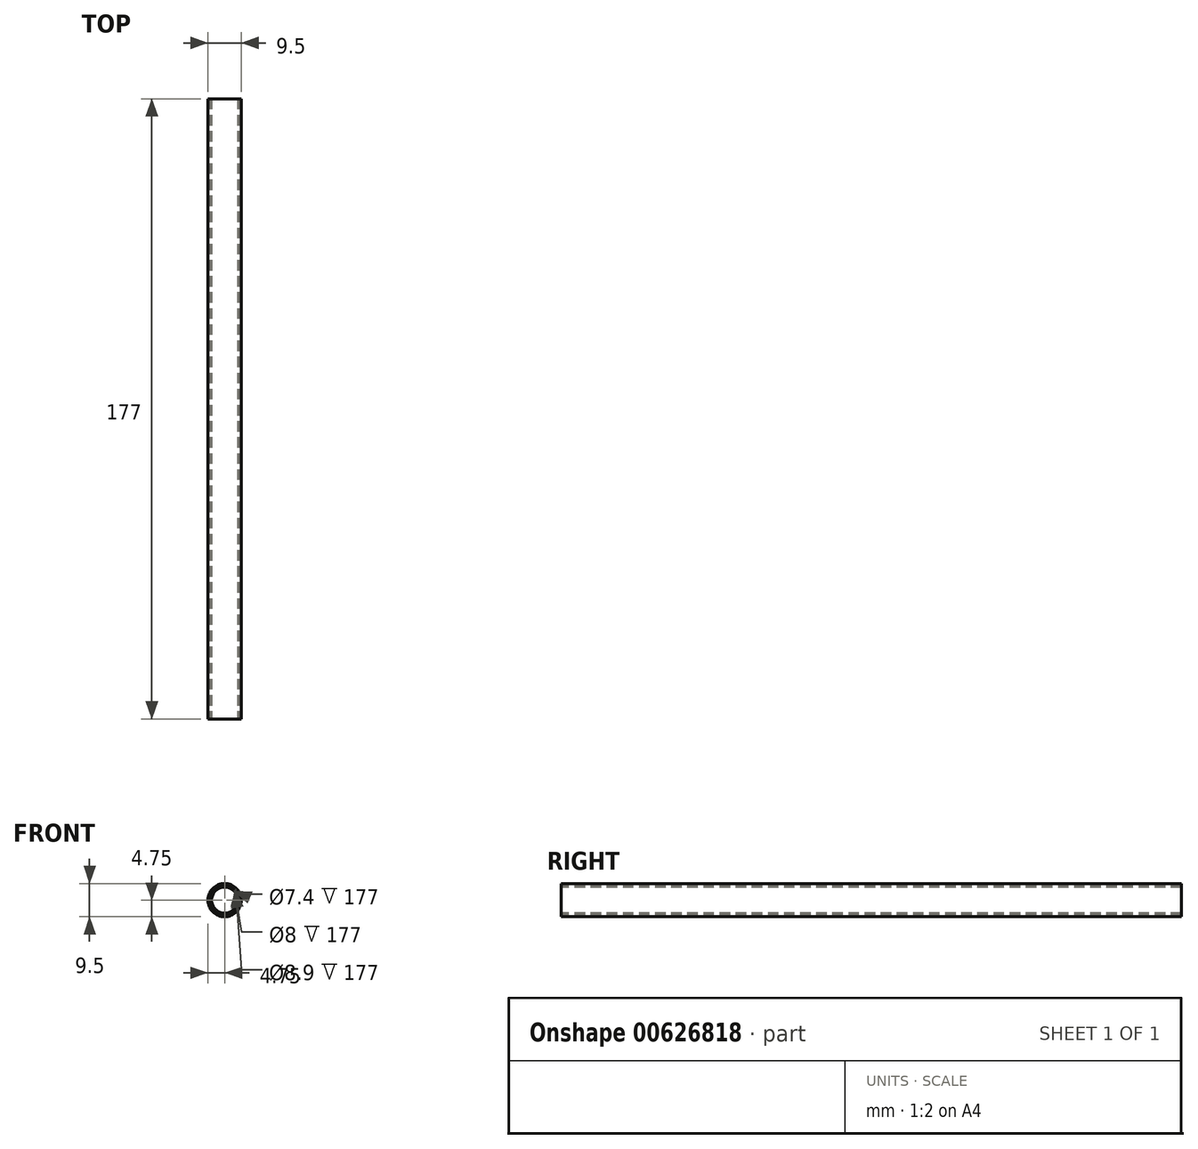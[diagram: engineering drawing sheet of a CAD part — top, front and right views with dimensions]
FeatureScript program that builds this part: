
annotation { "Feature Type Name" : "Feature", "Feature Type Description" : "" }
export const myFeature = defineFeature(function(context is Context, id is Id, definition is map)
    precondition{}
    {
        {
            var Q0;
            Q0=qCreatedBy(makeId("Front.planeOp"),FACE);
            var sketch = newSketch(context, id + "F0", { "sketchPlane" : qUnion([Q0])});
            skCircle(sketch, "E0", {"center": v(0, 0) * mm, "radius": 3.7 * mm});
            skCircle(sketch, "E1", {"center": v(0, 0) * mm, "radius": 4 * mm});
            skCircle(sketch, "E2", {"center": v(0, 0) * mm, "radius": 4.75 * mm});
            skCircle(sketch, "E3", {"center": v(0, 0) * mm, "radius": 4.45 * mm});
            skSolve(sketch);
        }
        {
            var Q0;
            Q0=makeQuery(id+"F0.imprint","IMPRINT",FACE,{"disambiguationData":[TD([[makeQuery(id+"F0.imprint","IMPRINT",EDGE,{"derivedFrom":sQuery(id+"F0.wireOp",EDGE,"E2")}),1.0]])]});
            extrude(context, id + "F1", {"entities" : qUnion([Q0]), "oppositeDirection" : true, "depth" : 177 * mm, "offsetDistance" : 25 * mm});
        }
        {
            var Q0;
            Q0=makeQuery(id+"F0.imprint","IMPRINT",FACE,{"disambiguationData":[TD([[makeQuery(id+"F0.imprint","IMPRINT",EDGE,{"derivedFrom":sQuery(id+"F0.wireOp",EDGE,"E0")}),-1.0]])]});
            extrude(context, id + "F2", {"entities" : qUnion([Q0]), "oppositeDirection" : true, "depth" : 177 * mm, "offsetDistance" : 25 * mm});
        }
        {
            var Q0;
            Q0=makeQuery(id+"F0.imprint","IMPRINT",FACE,{"disambiguationData":[TD([[makeQuery(id+"F0.imprint","IMPRINT",EDGE,{"derivedFrom":sQuery(id+"F0.wireOp",EDGE,"E1")}),-1.0]])]});
            extrude(context, id + "F3", {"entities" : qUnion([Q0]), "oppositeDirection" : true, "depth" : 177 * mm, "offsetDistance" : 25 * mm});
        }
    });
